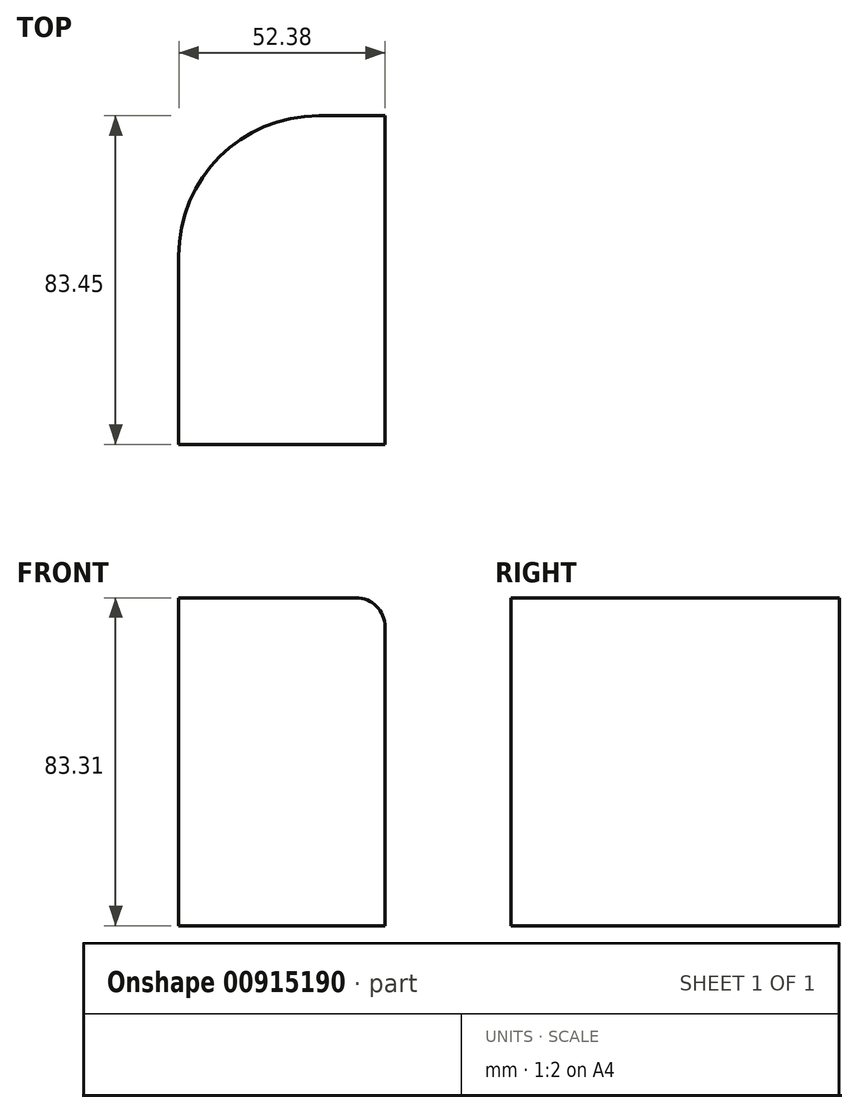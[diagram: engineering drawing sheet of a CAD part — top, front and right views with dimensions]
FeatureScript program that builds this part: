
annotation { "Feature Type Name" : "Feature", "Feature Type Description" : "" }
export const myFeature = defineFeature(function(context is Context, id is Id, definition is map)
    precondition{}
    {
        {
            var Q0;
            Q0=qCreatedBy(makeId("Top.planeOp"),FACE);
            var sketch = newSketch(context, id + "F0", { "sketchPlane" : qUnion([Q0])});
            skLineSegment(sketch, "E0.bottom", {"start": v(-119.8, 35.39) * mm, "end": v(-67.41, 35.39) * mm});
            skLineSegment(sketch, "E0.top", {"start": v(-119.8, -48.06) * mm, "end": v(-67.41, -48.06) * mm});
            skLineSegment(sketch, "E0.left", {"start": v(-119.8, 35.39) * mm, "end": v(-119.8, -48.06) * mm});
            skLineSegment(sketch, "E0.right", {"start": v(-67.41, 35.39) * mm, "end": v(-67.41, -48.06) * mm});
            skSolve(sketch);
        }
        {
            var Q0;
            Q0=makeQuery(id+"F0.imprint","IMPRINT",FACE,{"disambiguationData":[TD([[makeQuery(id+"F0.imprint","IMPRINT",EDGE,{"derivedFrom":sQuery(id+"F0.wireOp",EDGE,"E0.bottom")}),-1.0]])]});
            extrude(context, id + "F1", {"entities" : qUnion([Q0]), "depth" : 83.31 * mm, "offsetDistance" : 25.4 * mm});
        }
        {
            var Q0;
            Q0=makeQuery(id+"F1.opExtrude","CAP_EDGE",EDGE,{"disambiguationData":[OSD([sQuery(id+"F0.wireOp",EDGE,"E0.right")])],"isStart":false});
            fillet(context, id + "F2", {"entities" : qUnion([Q0]), "radius" : 7.36 * mm, "tangentPropagation" : true, "allowEdgeOverflow" : false});
        }
        {
            var Q0;
            Q0=makeQuery(id+"F1.opExtrude","SWEPT_EDGE",EDGE,{"disambiguationData":[OSD([sQuery(id+"F0.wireOp",EDGE,"E0.bottom"),sQuery(id+"F0.wireOp",EDGE,"E0.left")])]});
            fillet(context, id + "F3", {"entities" : qUnion([Q0]), "radius" : 35.57 * mm, "tangentPropagation" : true, "allowEdgeOverflow" : false});
        }
    });
